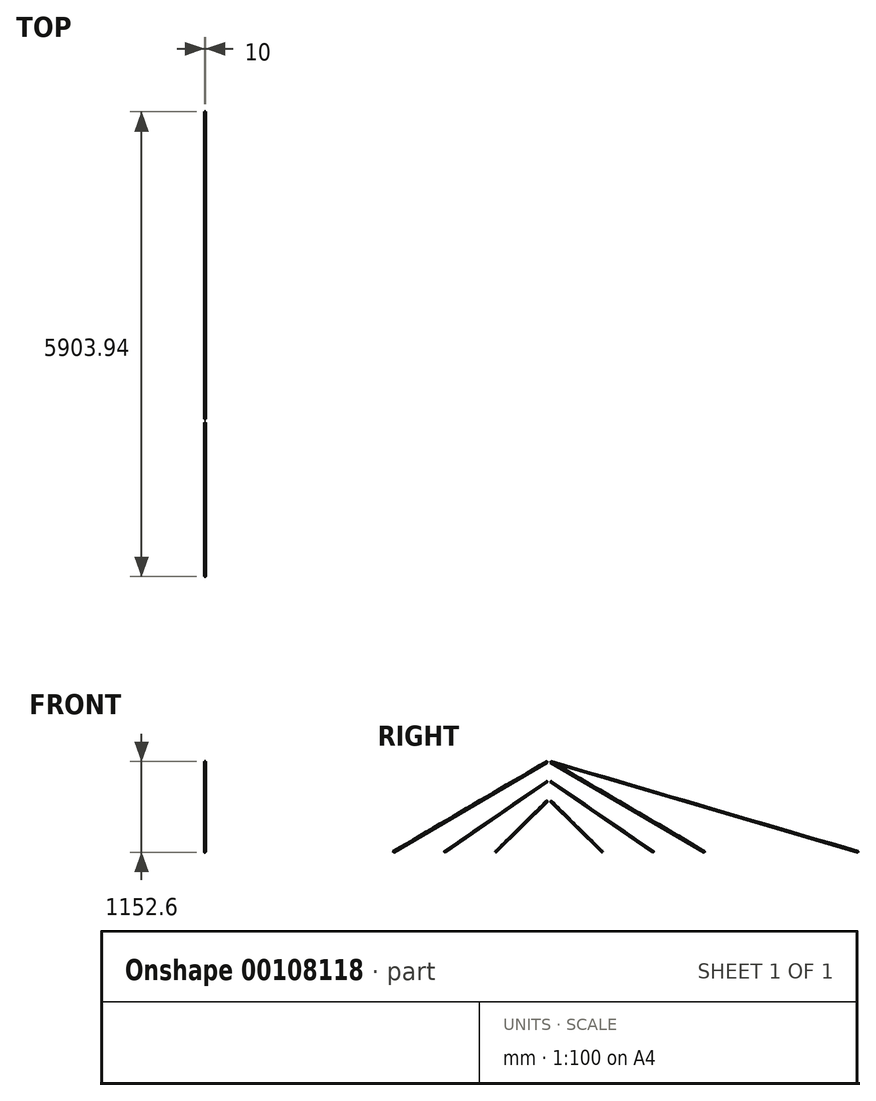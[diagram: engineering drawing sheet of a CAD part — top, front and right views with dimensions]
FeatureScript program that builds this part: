
annotation { "Feature Type Name" : "Feature", "Feature Type Description" : "" }
export const myFeature = defineFeature(function(context is Context, id is Id, definition is map)
    precondition{}
    {
        {
            assignVariable(context, id + "F0", {"name" : "Y1", "anyValue" : 3900});
        }
        {
            var Q0;
            Q0=qCreatedBy(makeId("Front.planeOp"),FACE);
            cPlane(context, id + "F1", {"entities" : qUnion([Q0]), "cplaneType" : CPlaneType.OFFSET, "offset" : (getVariable(context, 'Y1')) * mm, "width" : 150 * mm, "height" : 150 * mm});
        }
        {
            var Q0;
            Q0=qCreatedBy(id+"F1.planeOp",FACE);
            var sketch = newSketch(context, id + "F2", { "sketchPlane" : qUnion([Q0])});
            skPoint(sketch, "E0", {"position": v(0, 5800) * mm});
            skPoint(sketch, "E1", {"position": v(0, 0) * mm});
            skSolve(sketch);
        }
        {
            assignVariable(context, id + "F3", {"name" : "Y2", "anyValue" : 3900 / 2});
        }
        {
            var Q0;
            Q0=qCreatedBy(makeId("Front.planeOp"),FACE);
            cPlane(context, id + "F4", {"entities" : qUnion([Q0]), "cplaneType" : CPlaneType.OFFSET, "offset" : (getVariable(context, 'Y2')) * mm, "width" : 150 * mm, "height" : 150 * mm});
        }
        {
            var Q0;
            Q0=qCreatedBy(id+"F4.planeOp",FACE);
            var sketch = newSketch(context, id + "F5", { "sketchPlane" : qUnion([Q0])});
            skPoint(sketch, "E2", {"position": v(0, 4657) * mm});
            skSolve(sketch);
        }
        {
            var Q0;
            Q0=sQuery(id+"F2.wireOp",VERTEX,"E0");
            var Q1;
            Q1=sQuery(id+"F2.wireOp",VERTEX,"E1");
            var Q2;
            Q2=sQuery(id+"F5.wireOp",VERTEX,"E2");
            cPlane(context, id + "F6", {"entities" : qUnion([Q0, Q1, Q2]), "cplaneType" : CPlaneType.THREE_POINT, "offset" : 25 * mm, "width" : 150 * mm, "height" : 150 * mm});
        }
        {
            var Q0;
            Q0=qCreatedBy(id+"F6.planeOp",FACE);
            var sketch = newSketch(context, id + "F7", { "sketchPlane" : qUnion([Q0])});
            skPoint(sketch, "E3.0", {"position": v(3900, 5800) * mm});
            skPoint(sketch, "E4.0", {"position": v(1950, 4657) * mm});
            skLineSegment(sketch, "E5", {"start": v(3900, 5800) * mm, "end": v(1950, 4657) * mm});
            skLineSegment(sketch, "E6", {"start": v(3900, 5550) * mm, "end": v(2600, 4657) * mm});
            skLineSegment(sketch, "E7", {"start": v(3900, 5800) * mm, "end": v(0, 4657) * mm});
            skLineSegment(sketch, "E8", {"start": v(3900, 5300) * mm, "end": v(3250, 4657) * mm});
            skLineSegment(sketch, "E9", {"start": v(3950, 5800) * mm, "end": v(6096, 4657) * mm});
            skLineSegment(sketch, "E10", {"start": v(3950, 5550) * mm, "end": v(5381, 4657) * mm});
            skLineSegment(sketch, "E11", {"start": v(3950, 5300) * mm, "end": v(4666, 4657) * mm});
            skSolve(sketch);
        }
        {
            var Q0;
            Q0=sQuery(id+"F7.wireOp",VERTEX,"E3.0");
            var Q1;
            Q1=sQuery(id+"F7.wireOp",EDGE,"E5");
            cPlane(context, id + "F8", {"entities" : qUnion([Q0, Q1]), "cplaneType" : CPlaneType.LINE_POINT, "offset" : 25 * mm, "width" : 150 * mm, "height" : 150 * mm});
        }
        {
            var Q0;
            Q0=qCreatedBy(id+"F8.planeOp",FACE);
            var sketch = newSketch(context, id + "F9", { "sketchPlane" : qUnion([Q0])});
            skPoint(sketch, "E12.0", {"position": v(0, 3031.6) * mm});
            skCircle(sketch, "E13", {"center": v(0, 3031.6) * mm, "radius": 5 * mm});
            skSolve(sketch);
        }
        {
            var Q0;
            Q0=makeQuery(id+"F9.imprint","IMPRINT",FACE,{"disambiguationData":[TD([[makeQuery(id+"F9.imprint","IMPRINT",EDGE,{"derivedFrom":sQuery(id+"F9.wireOp",EDGE,"E13")}),1.0]])]});
            var Q1;
            Q1=sQuery(id+"F7.wireOp",EDGE,"E5");
            sweep(context, id + "F10", {"profiles" : qUnion([Q0]), "path" : qUnion([Q1])});
        }
        {
            var Q0;
            Q0=sQuery(id+"F7.wireOp",EDGE,"E7");
            var Q1;
            Q1=sQuery(id+"F7.wireOp",VERTEX,"E3.0");
            cPlane(context, id + "F11", {"entities" : qUnion([Q0, Q1]), "cplaneType" : CPlaneType.LINE_POINT, "offset" : 25 * mm, "width" : 150 * mm, "height" : 150 * mm});
        }
        {
            var Q0;
            Q0=qCreatedBy(id+"F11.planeOp",FACE);
            var sketch = newSketch(context, id + "F12", { "sketchPlane" : qUnion([Q0])});
            skPoint(sketch, "E14.0", {"position": v(0, 4469.02) * mm});
            skCircle(sketch, "E15", {"center": v(0, 4469.02) * mm, "radius": 5 * mm});
            skSolve(sketch);
        }
        {
            var Q0;
            Q0 = qSketchRegion(id + "F12", true);
            var Q1;
            Q1=sQuery(id+"F7.wireOp",EDGE,"E7");
            sweep(context, id + "F13", {"profiles" : qUnion([Q0]), "path" : qUnion([Q1])});
        }
        {
            var Q0;
            Q0=sQuery(id+"F7.wireOp",EDGE,"E6");
            var Q1;
            Q1=sQuery(id+"F7.wireOp",VERTEX,"E6.start");
            cPlane(context, id + "F14", {"entities" : qUnion([Q0, Q1]), "cplaneType" : CPlaneType.LINE_POINT, "offset" : 25 * mm, "width" : 150 * mm, "height" : 150 * mm});
        }
        {
            var Q0;
            Q0=qCreatedBy(id+"F14.planeOp",FACE);
            var sketch = newSketch(context, id + "F15", { "sketchPlane" : qUnion([Q0])});
            skPoint(sketch, "E16.0", {"position": v(0, 2366.46) * mm});
            skCircle(sketch, "E17", {"center": v(0, 2366.46) * mm, "radius": 5 * mm});
            skSolve(sketch);
        }
        {
            var Q0;
            Q0 = qSketchRegion(id + "F15", true);
            var Q1;
            Q1=sQuery(id+"F7.wireOp",EDGE,"E6");
            sweep(context, id + "F16", {"profiles" : qUnion([Q0]), "path" : qUnion([Q1])});
        }
        {
            var Q0;
            Q0=sQuery(id+"F7.wireOp",EDGE,"E8");
            var Q1;
            Q1=sQuery(id+"F7.wireOp",VERTEX,"E8.start");
            cPlane(context, id + "F17", {"entities" : qUnion([Q0, Q1]), "cplaneType" : CPlaneType.LINE_POINT, "offset" : 25 * mm, "width" : 150 * mm, "height" : 150 * mm});
        }
        {
            var Q0;
            Q0=qCreatedBy(id+"F17.planeOp",FACE);
            var sketch = newSketch(context, id + "F18", { "sketchPlane" : qUnion([Q0])});
            skPoint(sketch, "E18.0", {"position": v(0, 1025.15) * mm});
            skCircle(sketch, "E19", {"center": v(0, 1025.15) * mm, "radius": 5 * mm});
            skSolve(sketch);
        }
        {
            var Q0;
            Q0 = qSketchRegion(id + "F18", true);
            var Q1;
            Q1=sQuery(id+"F7.wireOp",EDGE,"E8");
            sweep(context, id + "F19", {"profiles" : qUnion([Q0]), "path" : qUnion([Q1])});
        }
        {
            var Q0;
            Q0=qCreatedBy(id+"F1.planeOp",FACE);
            cPlane(context, id + "F20", {"entities" : qUnion([Q0]), "cplaneType" : CPlaneType.OFFSET, "offset" : 25 * mm, "width" : 150 * mm, "height" : 150 * mm});
        }
        {
            var Q0;
            Q0=makeQuery(id+"F19.opSweep","SWEPT_BODY",BODY,{"disambiguationData":[OSD([sQuery(id+"F7.wireOp",EDGE,"E8"),sQuery(id+"F18.wireOp",EDGE,"E19")])]});
            var Q1;
            Q1=makeQuery(id+"F16.opSweep","SWEPT_BODY",BODY,{"disambiguationData":[OSD([sQuery(id+"F7.wireOp",EDGE,"E6"),sQuery(id+"F15.wireOp",EDGE,"E17")])]});
            var Q2;
            Q2=makeQuery(id+"F10.opSweep","SWEPT_BODY",BODY,{"disambiguationData":[OSD([sQuery(id+"F7.wireOp",EDGE,"E5"),sQuery(id+"F9.wireOp",EDGE,"E13")])]});
            var Q3;
            Q3=qCreatedBy(id+"F20.planeOp",FACE);
            mirror(context, id + "F21", {"entities" : qUnion([Q0, Q1, Q2]), "mirrorPlane" : qUnion([Q3])});
        }
    });
